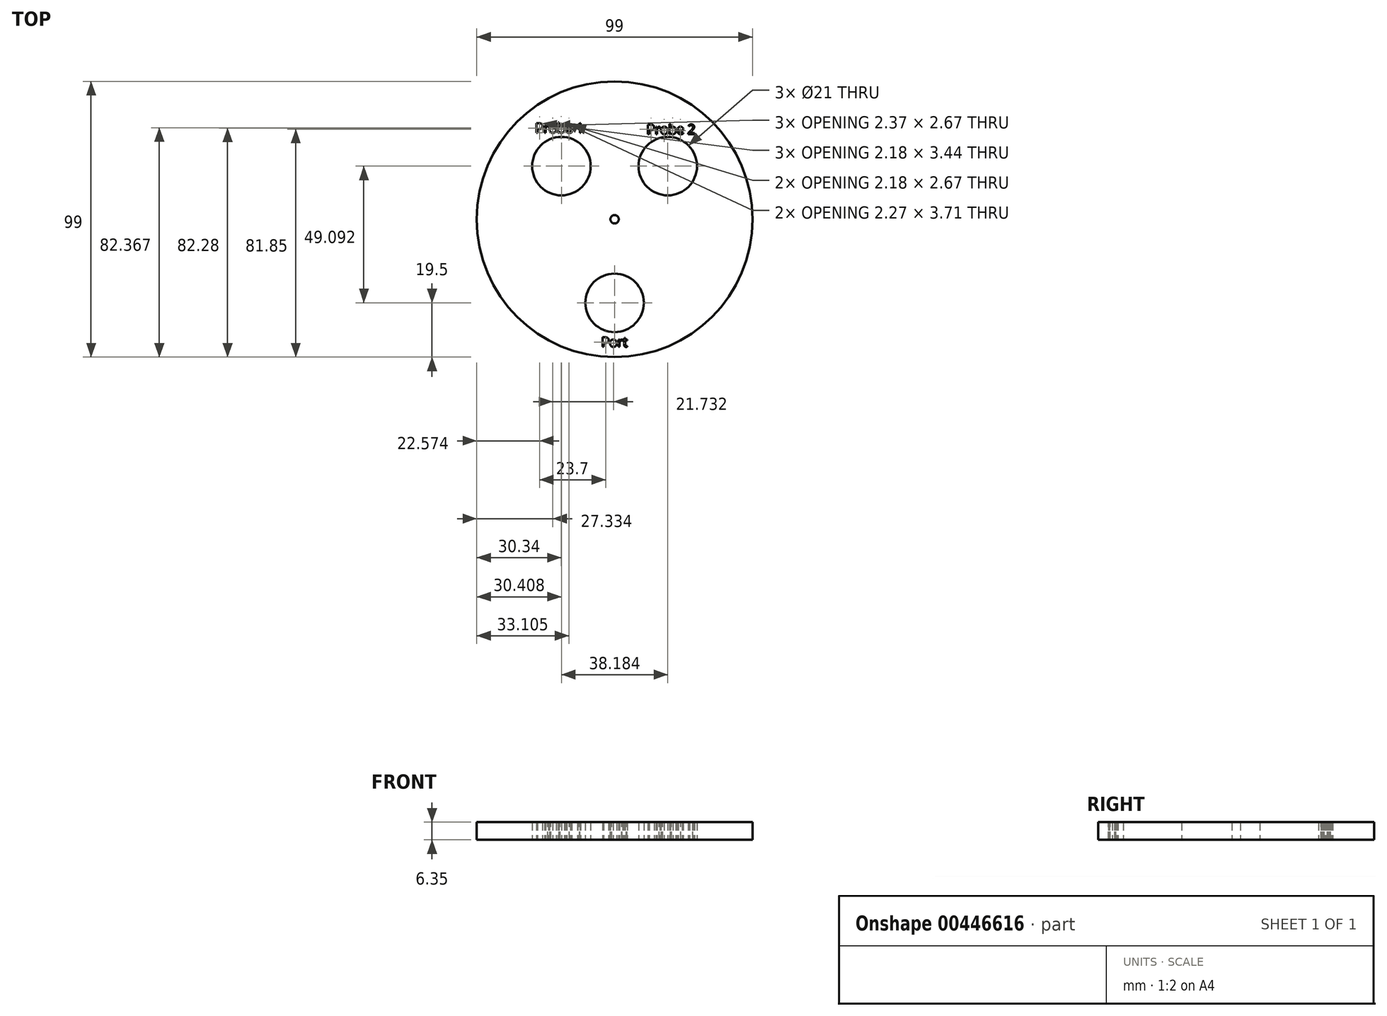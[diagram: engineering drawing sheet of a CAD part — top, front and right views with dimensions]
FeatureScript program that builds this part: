
annotation { "Feature Type Name" : "Feature", "Feature Type Description" : "" }
export const myFeature = defineFeature(function(context is Context, id is Id, definition is map)
    precondition{}
    {
        {
            var Q0;
            Q0=qCreatedBy(makeId("Top.planeOp"),FACE);
            var sketch = newSketch(context, id + "F0", { "sketchPlane" : qUnion([Q0])});
            skLineSegment(sketch, "E0", {"start": v(0, 0) * mm, "end": v(-19.1, 19.1) * mm, "construction": true});
            skCircle(sketch, "E1", {"center": v(-19.1, 19.1) * mm, "radius": 10.5 * mm});
            skLineSegment(sketch, "E2", {"start": v(0, 0) * mm, "end": v(19.1, 19.1) * mm, "construction": true});
            skCircle(sketch, "E3", {"center": v(19.1, 19.1) * mm, "radius": 10.5 * mm});
            skLineSegment(sketch, "E4", {"start": v(0, 0) * mm, "end": v(0, -30) * mm, "construction": true});
            skCircle(sketch, "E5", {"center": v(0, -30) * mm, "radius": 10.5 * mm});
            skCircle(sketch, "E6", {"center": v(0, 0) * mm, "radius": 1.5 * mm});
            skCircle(sketch, "E7", {"center": v(0, 0) * mm, "radius": 49.5 * mm});
            skText(sketch, "E8", { "text": "Probe 1", "fontName": "OpenSans-Regular.ttf"});
            skText(sketch, "E9", { "text": "Probe 2", "fontName": "OpenSans-Regular.ttf"});
            skText(sketch, "E10", { "text": "Port", "fontName": "OpenSans-Regular.ttf"});
            const initialGuessF0  = {"E8": [-0.02849, 0.03106, 1, 0, 0.00347], "E9": [0.01152, 0.0306, 1, 0, 0.00347], "E10": [-0.00479, -0.0458, 1, 0, 0.00347]};
            skSetInitialGuess(sketch, initialGuessF0);
            skSolve(sketch);
        }
        {
            var Q0;
            Q0 = qSketchRegion(id + "F0", true);
            extrude(context, id + "F1", {"entities" : qUnion([Q0]), "depth" : 6.35 * mm});
        }
    });
